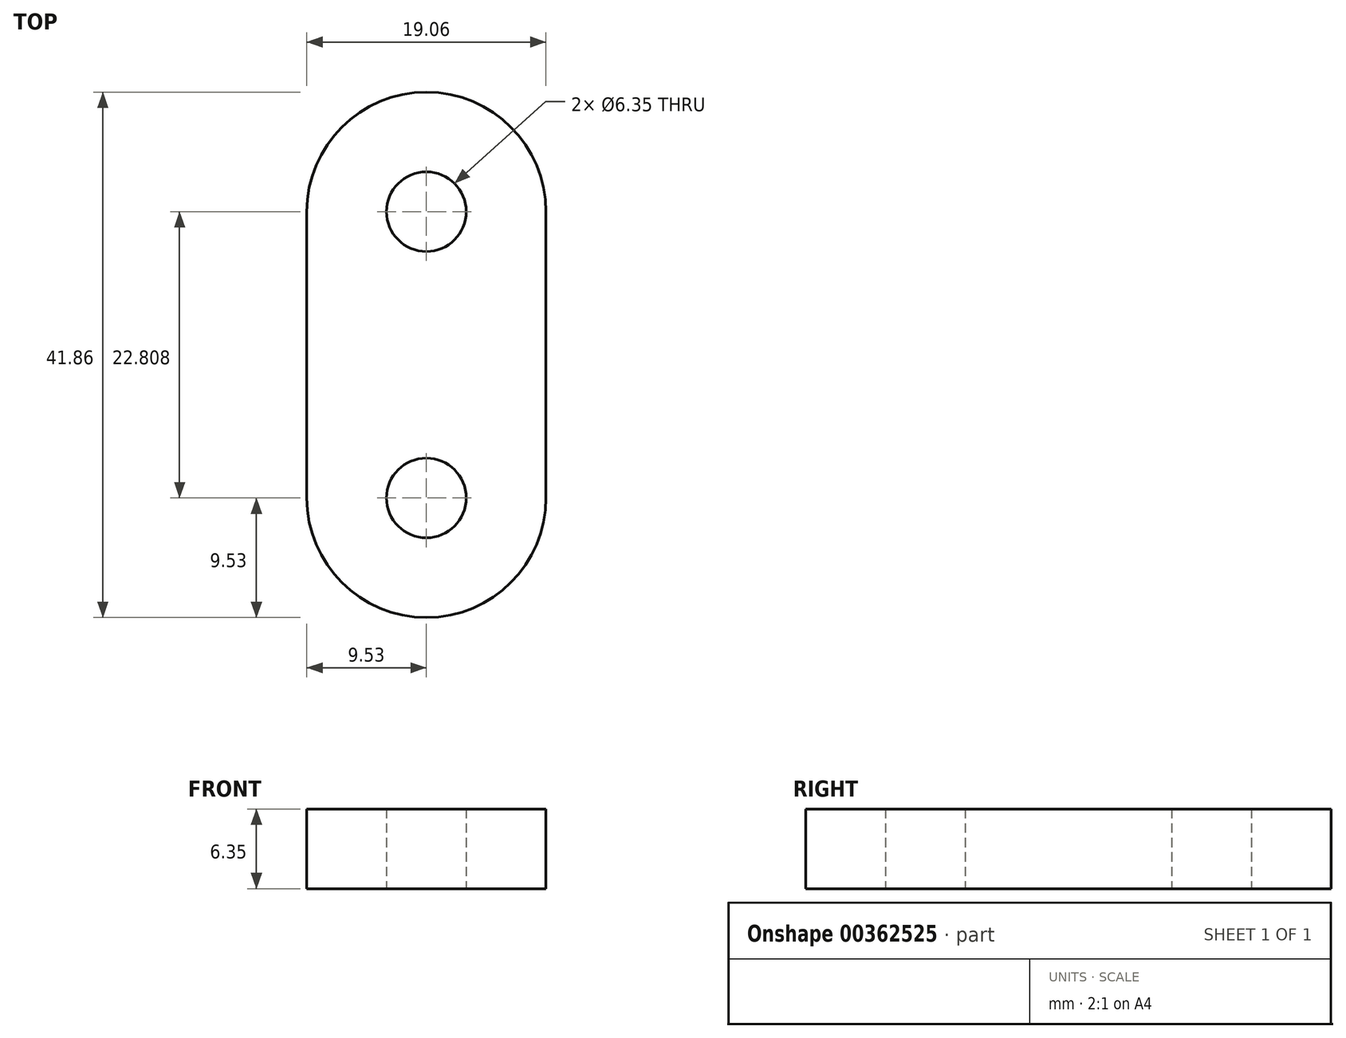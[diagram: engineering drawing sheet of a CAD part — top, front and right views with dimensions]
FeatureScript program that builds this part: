
annotation { "Feature Type Name" : "Feature", "Feature Type Description" : "" }
export const myFeature = defineFeature(function(context is Context, id is Id, definition is map)
    precondition{}
    {
        {
            var Q0;
            Q0=qCreatedBy(makeId("Top.planeOp"),FACE);
            var sketch = newSketch(context, id + "F0", { "sketchPlane" : qUnion([Q0])});
            skLineSegment(sketch, "E0", {"start": v(0, 0) * mm, "end": v(0, 22.8) * mm});
            skCircle(sketch, "E1", {"center": v(0, 22.8) * mm, "radius": 3.18 * mm});
            skCircle(sketch, "E2", {"center": v(0, 22.8) * mm, "radius": 9.53 * mm});
            skCircle(sketch, "E3", {"center": v(0, 0) * mm, "radius": 3.18 * mm});
            skCircle(sketch, "E4", {"center": v(0, 0) * mm, "radius": 9.53 * mm});
            skLineSegment(sketch, "E5", {"start": v(-9.53, 22.8) * mm, "end": v(-9.53, 0) * mm});
            skLineSegment(sketch, "E6", {"start": v(9.53, 22.8) * mm, "end": v(9.53, 0) * mm});
            skSolve(sketch);
        }
        {
            var Q0;
            Q0 = qSketchRegion(id + "F0", true);
            extrude(context, id + "F1", {"entities" : qUnion([Q0]), "depth" : 6.35 * mm});
        }
    });
